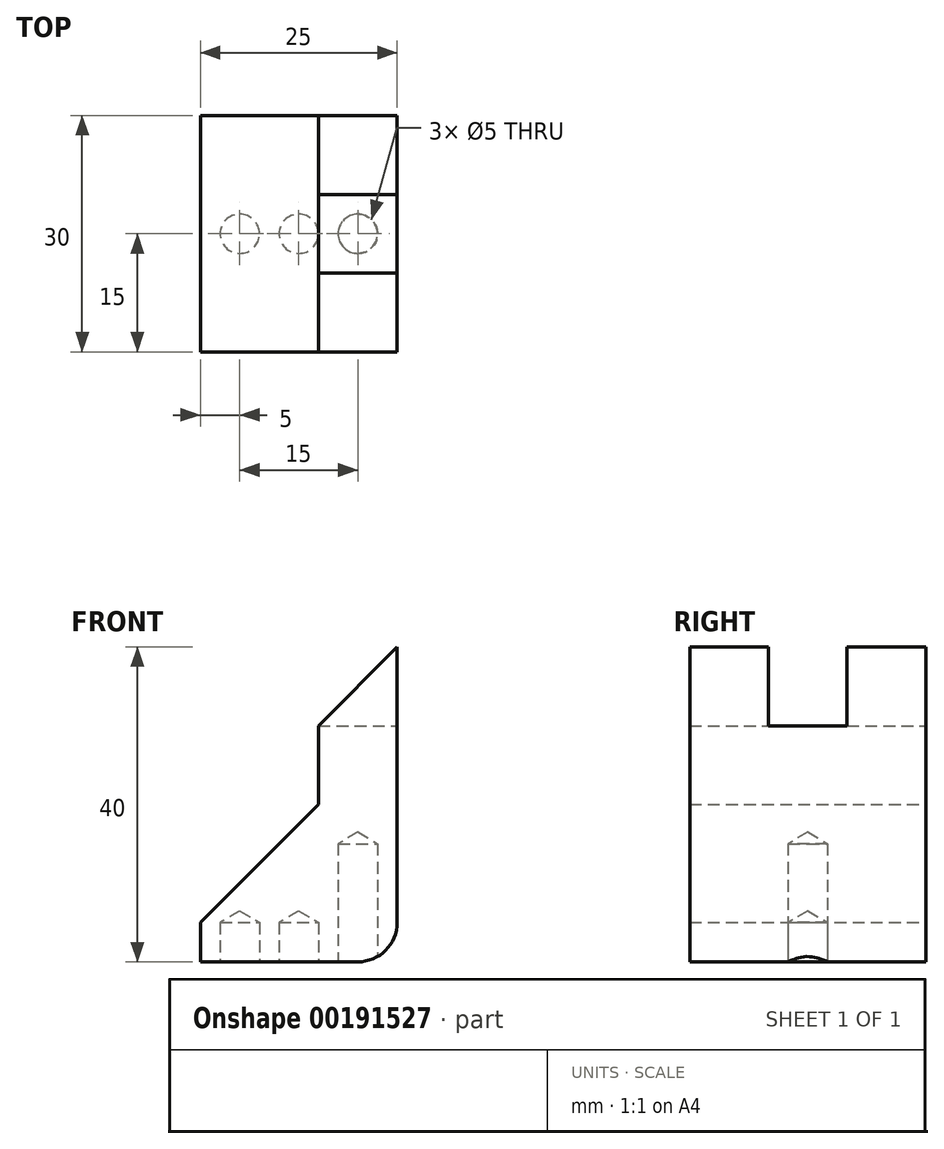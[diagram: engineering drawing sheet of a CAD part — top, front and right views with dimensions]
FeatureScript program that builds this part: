
annotation { "Feature Type Name" : "Feature", "Feature Type Description" : "" }
export const myFeature = defineFeature(function(context is Context, id is Id, definition is map)
    precondition{}
    {
        {
            var Q0;
            Q0=qCreatedBy(makeId("Front.planeOp"),FACE);
            var sketch = newSketch(context, id + "F5", { "sketchPlane" : qUnion([Q0])});
            skLineSegment(sketch, "E0", {"start": v(0, 0) * mm, "end": v(20, 0) * mm});
            skLineSegment(sketch, "E1", {"start": v(20, 0) * mm, "end": v(20, 20) * mm});
            skLineSegment(sketch, "E2", {"start": v(20, 20) * mm, "end": v(0, 0) * mm});
            skLineSegment(sketch, "E3", {"start": v(10, 0) * mm, "end": v(10, 10) * mm});
            skLineSegment(sketch, "E4", {"start": v(20, 0) * mm, "end": v(20, -10) * mm});
            skLineSegment(sketch, "E5", {"start": v(20, -10) * mm, "end": v(-5, -10) * mm});
            skLineSegment(sketch, "E6", {"start": v(-5, -10) * mm, "end": v(-5, -5) * mm});
            skLineSegment(sketch, "E7", {"start": v(20, 20) * mm, "end": v(-5, -5) * mm});
            skLineSegment(sketch, "E8", {"start": v(10, 10) * mm, "end": v(20, 10) * mm});
            skLineSegment(sketch, "E9", {"start": v(10, 10) * mm, "end": v(10, 20) * mm});
            skLineSegment(sketch, "E10", {"start": v(20, 20) * mm, "end": v(20, 30) * mm});
            skLineSegment(sketch, "E11", {"start": v(20, 30) * mm, "end": v(10, 20) * mm});
            skLineSegment(sketch, "E12", {"start": v(10, 20) * mm, "end": v(20, 20) * mm});
            skSolve(sketch);
        }
        {
            var Q0;
            {var subQ2=sQuery(id+"F5.wireOp",EDGE,"E9");Q0=makeQuery(id+"F5.imprint","IMPRINT",FACE,{"disambiguationData":[TD([[makeQuery(id+"F5.imprint","IMPRINT",EDGE,{"derivedFrom":subQ2}),-1.0]])]});}
            var Q1;
            {var subQ3=sQuery(id+"F5.wireOp",EDGE,"E8");Q1=makeQuery(id+"F5.imprint","IMPRINT",FACE,{"disambiguationData":[TD([[makeQuery(id+"F5.imprint","IMPRINT",EDGE,{"derivedFrom":subQ3}),1.0]])]});}
            var Q2;
            {var subQ3=sQuery(id+"F5.wireOp",EDGE,"E3");Q2=makeQuery(id+"F5.imprint","IMPRINT",FACE,{"disambiguationData":[TD([[makeQuery(id+"F5.imprint","IMPRINT",EDGE,{"derivedFrom":subQ3}),-1.0]])]});}
            var Q3;
            {var subQ3=sQuery(id+"F5.wireOp",EDGE,"E3");Q3=makeQuery(id+"F5.imprint","IMPRINT",FACE,{"disambiguationData":[TD([[makeQuery(id+"F5.imprint","IMPRINT",EDGE,{"derivedFrom":subQ3}),1.0]])]});}
            var Q4;
            {var subQ0=sQuery(id+"F5.wireOp",EDGE,"E4");Q4=makeQuery(id+"F5.imprint","IMPRINT",FACE,{"disambiguationData":[TD([[makeQuery(id+"F5.imprint","IMPRINT",EDGE,{"derivedFrom":subQ0}),-1.0]])]});}
            extrude(context, id + "F0", {"entities" : qUnion([Q0, Q1, Q2, Q3, Q4]), "depth" : 30 * mm});
        }
        {
            var Q0;
            Q0=makeQuery(id+"F5.imprint","IMPRINT",FACE,{"disambiguationData":[TD([[makeQuery(id+"F5.imprint","IMPRINT",EDGE,{"derivedFrom":sQuery(id+"F5.wireOp",EDGE,"E10")}),1.0]])]});
            extrude(context, id + "F1", {"entities" : qUnion([Q0]), "operationType" : NewBodyOperationType.ADD, "depth" : 10 * mm});
        }
        {
            var Q0;
            Q0=makeQuery(id+"F0.opExtrude","CAP_FACE",FACE,{"disambiguationData":[OSD([sQuery(id+"F5.wireOp",EDGE,"E1"),sQuery(id+"F5.wireOp",EDGE,"E4"),sQuery(id+"F5.wireOp",EDGE,"E5"),sQuery(id+"F5.wireOp",EDGE,"E6"),sQuery(id+"F5.wireOp",EDGE,"E7"),sQuery(id+"F5.wireOp",EDGE,"E9"),sQuery(id+"F5.wireOp",EDGE,"E12")])],"isStart":false});
            var sketch = newSketch(context, id + "F6", { "sketchPlane" : qUnion([Q0])});
            skLineSegment(sketch, "E13", {"start": v(20, 20) * mm, "end": v(20, 30) * mm});
            skLineSegment(sketch, "E14", {"start": v(20, 30) * mm, "end": v(10, 20) * mm});
            skLineSegment(sketch, "E15", {"start": v(10, 20) * mm, "end": v(10, 20) * mm});
            skSolve(sketch);
        }
        {
            var Q0;
            Q0 = qSketchRegion(id + "F6", true);
            var Q1;
            Q1=makeQuery(id+"F6.imprint","IMPRINT",FACE,{"disambiguationData":[TD([[makeQuery(id+"F6.imprint","IMPRINT",EDGE,{"derivedFrom":sQuery(id+"F6.wireOp",EDGE,"E13")}),1.0]])]});
            extrude(context, id + "F7", {"entities" : qUnion([Q0, Q1]), "operationType" : NewBodyOperationType.ADD, "oppositeDirection" : true, "depth" : 10 * mm});
        }
        {
            var Q0;
            Q0=makeQuery(id+"F0.opExtrude","SWEPT_FACE",FACE,{"disambiguationData":[OSD([sQuery(id+"F5.wireOp",EDGE,"E5")])]});
            var sketch = newSketch(context, id + "F2", { "sketchPlane" : qUnion([Q0])});
            skPoint(sketch, "E16", {"position": v(7.5, 15) * mm});
            skPoint(sketch, "E16.positionSnap0", {"position": v(7.5, 0) * mm});
            skPoint(sketch, "E16.positionSnap1", {"position": v(-5, 15) * mm});
            skLineSegment(sketch, "E17", {"start": v(-5, 15) * mm, "end": v(20, 15) * mm});
            skLineSegment(sketch, "E18", {"start": v(-5, 15) * mm, "end": v(0, 15) * mm});
            skLineSegment(sketch, "E19", {"start": v(20, 15) * mm, "end": v(15, 15) * mm});
            skPoint(sketch, "E20", {"position": v(0, 15) * mm});
            skPoint(sketch, "E21", {"position": v(15, 15) * mm});
            skSolve(sketch);
        }
        {
            var Q0;
            Q0=sQuery(id+"F2.wireOp",VERTEX,"E21");
            var Q1;
            Q1=makeQuery(id+"F0.opExtrude","SWEPT_BODY",BODY,{"disambiguationData":[OSD([sQuery(id+"F5.wireOp",EDGE,"E1"),sQuery(id+"F5.wireOp",EDGE,"E4"),sQuery(id+"F5.wireOp",EDGE,"E5"),sQuery(id+"F5.wireOp",EDGE,"E6"),sQuery(id+"F5.wireOp",EDGE,"E7"),sQuery(id+"F5.wireOp",EDGE,"E9"),sQuery(id+"F5.wireOp",EDGE,"E12")])]});
            hole(context, id + "F3", {"style" : HoleStyle.SIMPLE, "endStyle" : HoleEndStyle.BLIND, "holeDiameter" : 5 * mm, "holeDepth" : 15 * mm, "locations" : qUnion([Q0]), "scope" : qUnion([Q1])});
        }
        {
            var Q0;
            Q0=sQuery(id+"F2.wireOp",VERTEX,"E16");
            var Q1;
            Q1=sQuery(id+"F2.wireOp",VERTEX,"E20");
            var Q2;
            Q2=makeQuery(id+"F0.opExtrude","SWEPT_BODY",BODY,{"disambiguationData":[OSD([sQuery(id+"F5.wireOp",EDGE,"E1"),sQuery(id+"F5.wireOp",EDGE,"E4"),sQuery(id+"F5.wireOp",EDGE,"E5"),sQuery(id+"F5.wireOp",EDGE,"E6"),sQuery(id+"F5.wireOp",EDGE,"E7"),sQuery(id+"F5.wireOp",EDGE,"E9"),sQuery(id+"F5.wireOp",EDGE,"E12")])]});
            hole(context, id + "F8", {"style" : HoleStyle.SIMPLE, "endStyle" : HoleEndStyle.BLIND, "holeDiameter" : 5 * mm, "holeDepth" : 5 * mm, "locations" : qUnion([Q0, Q1]), "scope" : qUnion([Q2])});
        }
        {
            var Q0;
            Q0=makeQuery(id+"F0.opExtrude","SWEPT_EDGE",EDGE,{"disambiguationData":[OSD([sQuery(id+"F5.wireOp",EDGE,"E4"),sQuery(id+"F5.wireOp",EDGE,"E5")])]});
            fillet(context, id + "F4", {"entities" : qUnion([Q0]), "radius" : 5 * mm, "tangentPropagation" : true, "allowEdgeOverflow" : false});
        }
    });
